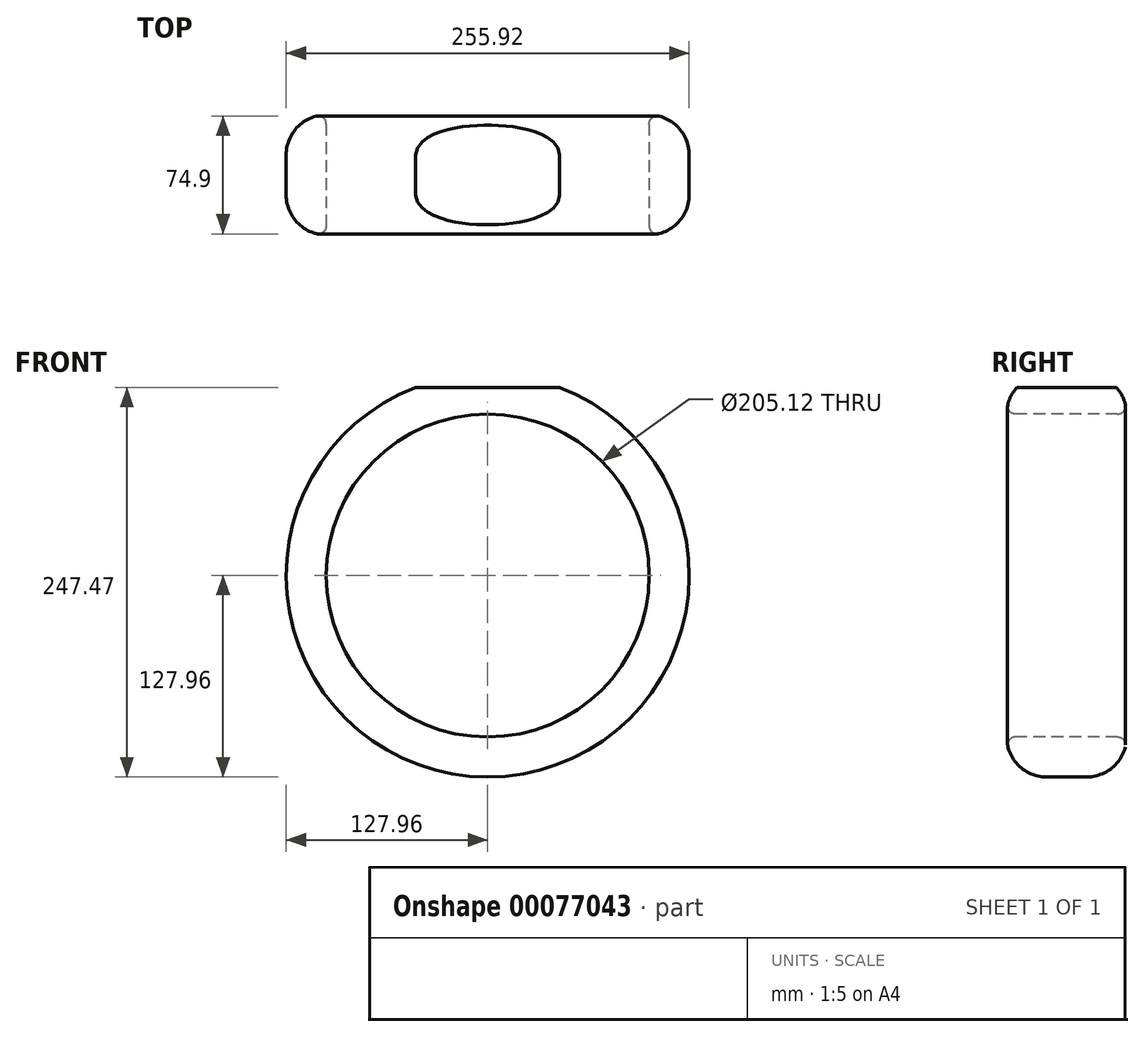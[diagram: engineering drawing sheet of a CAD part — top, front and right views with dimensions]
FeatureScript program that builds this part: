
annotation { "Feature Type Name" : "Feature", "Feature Type Description" : "" }
export const myFeature = defineFeature(function(context is Context, id is Id, definition is map)
    precondition{}
    {
        {
            var Q0;
            Q0=qCreatedBy(makeId("Front.planeOp"),FACE);
            var sketch = newSketch(context, id + "F0", { "sketchPlane" : qUnion([Q0])});
            skCircle(sketch, "E0", {"center": v(0, 0) * mm, "radius": 127.96 * mm});
            skSolve(sketch);
        }
        {
            var Q0;
            Q0=makeQuery(id+"F0.imprint","IMPRINT",FACE,{"disambiguationData":[TD([[makeQuery(id+"F0.imprint","IMPRINT",EDGE,{"derivedFrom":sQuery(id+"F0.wireOp",EDGE,"E0")}),1.0]])]});
            extrude(context, id + "F1", {"entities" : qUnion([Q0]), "depth" : 76.2 * mm});
        }
        {
            var Q0;
            Q0=makeQuery(id+"F1.opExtrude","CAP_EDGE",EDGE,{"disambiguationData":[OSD([sQuery(id+"F0.wireOp",EDGE,"E0")])],"isStart":false});
            var Q1;
            Q1=makeQuery(id+"F1.opExtrude","CAP_EDGE",EDGE,{"disambiguationData":[OSD([sQuery(id+"F0.wireOp",EDGE,"E0")])],"isStart":true});
            fillet(context, id + "F2", {"entities" : qUnion([Q0, Q1]), "radius" : 25.4 * mm, "tangentPropagation" : true, "allowEdgeOverflow" : false});
        }
        {
            var Q0;
            Q0=makeQuery(id+"F1.opExtrude","CAP_FACE",FACE,{"disambiguationData":[OSD([sQuery(id+"F0.wireOp",EDGE,"E0")])],"isStart":false});
            extrude(context, id + "F3", {"entities" : qUnion([Q0]), "operationType" : NewBodyOperationType.REMOVE, "oppositeDirection" : true, "depth" : 101.6 * mm});
        }
        {
            var Q0;
            Q0=makeQuery(id+"F3.boolean.opBoolean","COPY",FACE,{"derivedFrom":makeQuery(id+"F3.opExtrude","SWEPT_FACE",FACE,{"disambiguationData":[OSD([sQuery(id+"F0.wireOp",EDGE,"E0")])]})});
            fillet(context, id + "F4", {"entities" : qUnion([Q0]), "radius" : 5.08 * mm, "tangentPropagation" : true, "allowEdgeOverflow" : false});
        }
        {
            var Q0;
            Q0=qCreatedBy(makeId("Front.planeOp"),FACE);
            var sketch = newSketch(context, id + "F5", { "sketchPlane" : qUnion([Q0])});
            skLineSegment(sketch, "E1.bottom", {"start": v(-99.63, 151.12) * mm, "end": v(107.3, 151.12) * mm});
            skLineSegment(sketch, "E1.top", {"start": v(-99.63, 119.5) * mm, "end": v(107.3, 119.5) * mm});
            skLineSegment(sketch, "E1.left", {"start": v(-99.63, 151.12) * mm, "end": v(-99.63, 119.5) * mm});
            skLineSegment(sketch, "E1.right", {"start": v(107.3, 151.12) * mm, "end": v(107.3, 119.5) * mm});
            skSolve(sketch);
        }
        {
            var Q0;
            Q0=makeQuery(id+"F5.imprint","IMPRINT",FACE,{"disambiguationData":[TD([[makeQuery(id+"F5.imprint","IMPRINT",EDGE,{"derivedFrom":sQuery(id+"F5.wireOp",EDGE,"E1.bottom")}),-1.0]])]});
            extrude(context, id + "F6", {"entities" : qUnion([Q0]), "operationType" : NewBodyOperationType.REMOVE, "depth" : 101.6 * mm});
        }
    });
